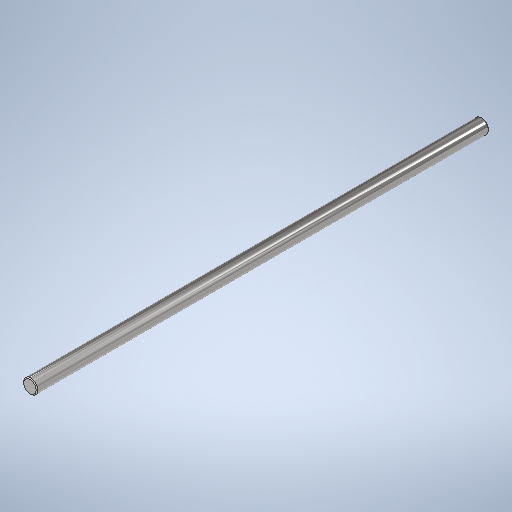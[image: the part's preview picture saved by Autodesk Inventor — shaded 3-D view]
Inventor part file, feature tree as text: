
AUTODESK INVENTOR PART (.ipt)
format: ipt  version: 2025.2 (Build 292293000, 293)  size: 261,120 bytes
history: native  units: mm
features: extrude x1, chamfer x1, sketch x1
ambient origin geometry x8: Origin, YZ Plane, XZ Plane, XY Plane, X Axis, Y Axis, Z Axis, Center Point
bodies: Solid1 (feature_tree)
feature tree (3):
  extrude  "Extrusion1"  Depth=250.0mm TaperAngle=0.0deg
  chamfer  "Chamfer1"  Distance=0.5mm Angle=45.0deg
  sketch  "Sketch1"  dims[d0=8.0mm d1=250.0mm d2=0.0mm d3=0.5mm d4=2.0mm d5=45.0deg]
